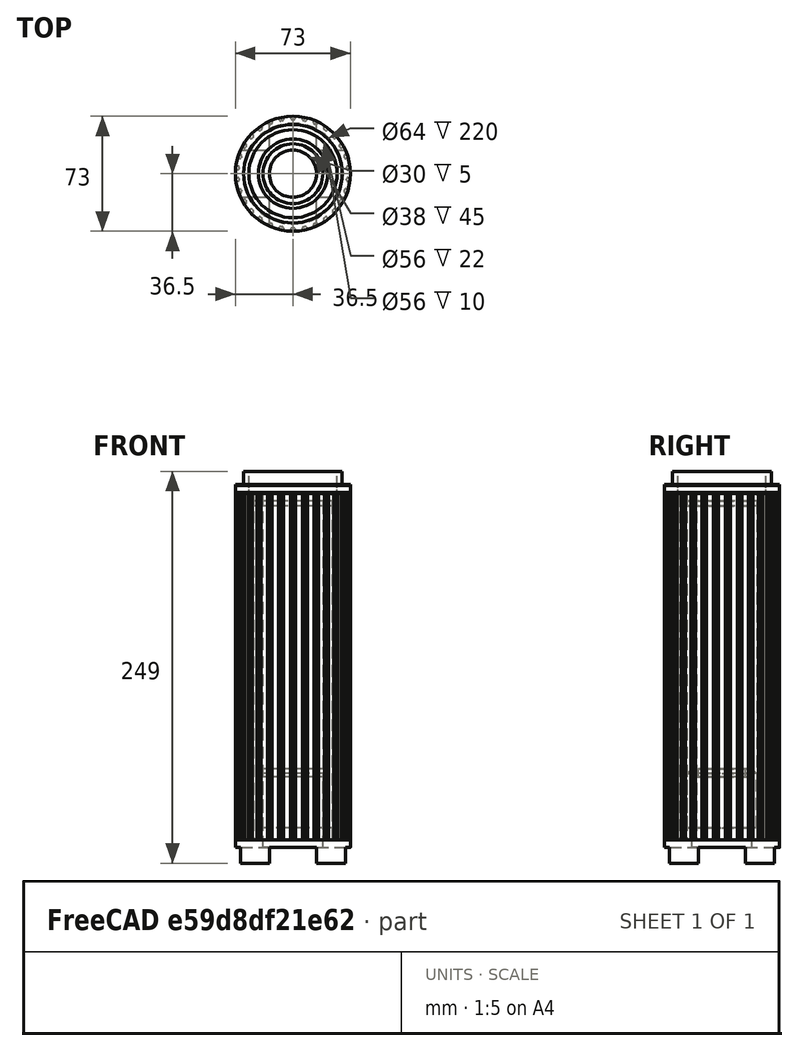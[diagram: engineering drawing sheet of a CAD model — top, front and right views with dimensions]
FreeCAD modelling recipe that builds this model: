
FCSTD DOCUMENT  (FreeCAD 0.15R4671 (Git))
Label: pica-small-v4
License: All rights reserved
LicenseURL: http://en.wikipedia.org/wiki/All_rights_reserved
objects: Part::Cylinder×14, Drawing::FeatureView×10, Part::Cut×7, Part::MultiFuse×6, Drawing::FeatureViewPart×6, Part::Box×2, Part::Part2DObjectPython×1, PartDesign::Pad×1, Drawing::FeaturePage×1, Part::Chamfer×1
note: 33 computed .brp shape members not serialized (recipe doc carries the construction recipe); baked Part::Feature solids carry a one-line shape summary decoded from their .brp

FEATURE [Part::Part2DObjectPython] InvoluteGear  # Draft 2D object (typed FeaturePython)
  ExternalGear = true
  HighPrecision = true
  Modules = 2.5
  NumberOfTeeth = 30
  PressureAngle = 20
FEATURE [PartDesign::Pad] Pad
  Length = 220
  Length2 = 100
  Sketch = -> InvoluteGear
  Type = 0
FEATURE [Part::Cylinder] Cylinder
  Angle = 360
  Height = 240
  Placement = pos=(0,0,-10) rot=(0,0,1;0rad)
  Radius = 32
FEATURE [Part::Cut] Cut  label="Final"
  Base = -> Pad
  Tool = -> Cylinder
FEATURE [Part::Cylinder] Cylinder001
  Angle = 360
  Height = 400
  Radius = 36.5
FEATURE [Part::Cylinder] Cylinder002
  Angle = 360
  Height = 400
  Radius = 100
FEATURE [Part::Cut] Cut001
  Base = -> Cylinder002
  Tool = -> Cylinder001
FEATURE [Part::Cut] Cut002  label="Shade"
  Base = -> Cut
  Placement = pos=(0,0,15) rot=(0,0,1;0rad)
  Tool = -> Cut001
FEATURE [Part::Cylinder] Cylinder003
  Angle = 360
  Height = 15
  Radius = 36.5
FEATURE [Part::Cylinder] Cylinder004
  Angle = 360
  Height = 22.5
  Radius = 31.3
FEATURE [Part::MultiFuse] Fusion  label="Base Fusion"
  Shapes = -> [Cylinder004,Cylinder003]
FEATURE [Drawing::FeatureViewPart] FrontView  label="Shade Side"
  Direction = (0,-1,0)
  HiddenWidth = 0.15
  LineWidth = 0.35
  Rotation = 90
  ShowHiddenLines = true
  ShowSmoothLines = false
  Source = -> Cut002
  Tolerance = 0.05
  ViewResult = <blob: 104580 chars omitted>
  Visible = true
  X = 80
  Y = 270
FEATURE [Drawing::FeatureViewPart] View001  label="Shade Top"
  Direction = (0,0,1)
  HiddenWidth = 0.15
  LineWidth = 0.35
  Rotation = 0
  ShowHiddenLines = false
  ShowSmoothLines = false
  Source = -> Cut002
  Tolerance = 0.05
  ViewResult = <blob: 17331 chars omitted>
  Visible = true
  X = 300
  Y = 80
FEATURE [Drawing::FeatureView] dim006  label="Base Radius"
  Rotation = 0
  ViewResult = <g   >\n <circle cx ="300.000000" cy ="170.000000" r="0.500000" stroke="none" fill="rgb(0,0,0)" /> \n<line x1="255.718312" y1="135.631286" x2="300.000000" y2="170.000000" style="stroke:rgb(0,0,0);stroke-width:0.30" />\n<polygon points="275.273643,150.808927 277.030448,153.438307 278.433561,153.261461 278.256715,151.858348" style="fill:rgb(0,0,0);stroke:rgb(0,0,0);stroke-width:0" />\n<line x1="255.718312" y1="135.631286" x2="231.639949" y2="135.631286" style="stroke:rgb(0,0,0);stroke-width:0.30" />\n<text x="219.448373" y="136.850443" font-family="Arial" font-size="3.6" fill="rgb(0,0,0)" text-anchor="inherit"  >R31.3</text>\n<!--31.3-->\n<!--R%3.3f-->\n</g> 
  Visible = true
  X = 0
  Y = 0
FEATURE [Drawing::FeatureView] centerLines
  Rotation = 0
  ViewResult = <g  transform="scale(1.000000,1.000000)" stroke="rgb(0,0,0)"  stroke-width="0.300000" >\n<path d="M 300.000000,170.000000 L 300.000000,168.000000 M 300.000000,166.000000 L 300.000000,160.000000 M 300.000000,158.000000 L 300.000000,156.000000 "/>\n<path d="M 300.000000,170.000000 L 302.000000,170.000000 M 304.000000,170.000000 L 310.000000,170.000000 M 312.000000,170.000000 L 314.000000,170.000000 "/>\n<path d="M 300.000000,170.000000 L 300.000000,172.000000 M 300.000000,174.000000 L 300.000000,180.000000 M 300.000000,182.000000 L 300.000000,184.000000 "/>\n<path d="M 300.000000,170.000000 L 298.000000,170.000000 M 296.000000,170.000000 L 290.000000,170.000000 M 288.000000,170.000000 L 286.000000,170.000000 "/>\n</g> 
  Visible = true
  X = 0
  Y = 0
FEATURE [Drawing::FeatureView] centerLines001
  Rotation = 0
  ViewResult = <g  transform="scale(1.000000,1.000000)" stroke="rgb(0,0,0)"  stroke-width="0.300000" >\n<path d="M 300.000000,80.000000 L 300.000000,82.000000 M 300.000000,84.000000 L 300.000000,90.000000 M 300.000000,92.000000 L 300.000000,94.000000 "/>\n<path d="M 300.000000,80.000000 L 302.000000,80.000000 M 304.000000,80.000000 L 310.000000,80.000000 M 312.000000,80.000000 L 314.000000,80.000000 "/>\n<path d="M 300.000000,80.000000 L 300.000000,78.000000 M 300.000000,76.000000 L 300.000000,70.000000 M 300.000000,68.000000 L 300.000000,66.000000 "/>\n<path d="M 300.000000,80.000000 L 298.000000,80.000000 M 296.000000,80.000000 L 290.000000,80.000000 M 288.000000,80.000000 L 286.000000,80.000000 "/>\n</g> 
  Visible = true
  X = 0
  Y = 0
FEATURE [Drawing::FeatureView] dim007  label="Shade Radius"
  Rotation = 0
  ViewResult = <g   >\n <circle cx ="300.000000" cy ="80.000000" r="0.500000" stroke="none" fill="rgb(0,0,0)" /> \n<line x1="340.917441" y1="111.884102" x2="300.000000" y2="80.000000" style="stroke:rgb(0,0,0);stroke-width:0.30" />\n<polygon points="325.241495,99.668933 323.489759,97.036174 322.086308,97.210316 322.260451,98.613767" style="fill:rgb(0,0,0);stroke:rgb(0,0,0);stroke-width:0" />\n<line x1="340.917441" y1="111.884102" x2="365.557939" y2="111.884102" style="stroke:rgb(0,0,0);stroke-width:0.30" />\n<text x="369.473360" y="112.835313" font-family="Arial" font-size="3.6" fill="rgb(0,0,0)" text-anchor="inherit"  >R32</text>\n<!--32.0-->\n<!--R%3.3f-->\n</g> 
  Visible = true
  X = 0
  Y = 0
FEATURE [Part::Cylinder] Cylinder005
  Angle = 360
  Height = 90
  Radius = 15
FEATURE [Part::Cylinder] Cylinder006
  Angle = 360
  Height = 55
  Radius = 19
FEATURE [Part::MultiFuse] Fusion002  label="Fixture Mount"
  Shapes = -> [Cylinder005,Cylinder006]
FEATURE [Drawing::FeatureViewPart] View004  label="Base Top"
  Direction = (0,0,1)
  HiddenWidth = 0.15
  LineWidth = 0.35
  Rotation = 0
  ShowHiddenLines = false
  ShowSmoothLines = false
  Tolerance = 0.05
  ViewResult = <g id="Base Top"\n   transform="rotate(0,300,170) translate(300,170) scale(1,1)"\n  >\n<g   stroke="rgb(0, 0, 0)"\n   stroke-width="0.35"\n   stroke-linecap="butt"\n   stroke-linejoin="miter"\n   fill="none"\n   transform="scale(1,-1)"\n  >\n<circle cx ="0" cy ="0" r ="23.3" /><circle cx ="0" cy ="0" r ="15" /><circle cx ="0" cy ="0" r ="31.3" /><circle cx ="0" cy ="0" r ="36.5" /></g>\n</g>
  Visible = true
  X = 300
  Y = 170
FEATURE [Drawing::FeatureViewPart] View005  label="Base Side"
  Direction = (0,-1,0)
  HiddenWidth = 0.15
  LineWidth = 0.35
  Rotation = 90
  ShowHiddenLines = false
  ShowSmoothLines = false
  Tolerance = 0.05
  ViewResult = <blob: 2600 chars omitted>
  Visible = true
  X = 80
  Y = 270
FEATURE [Drawing::FeatureViewPart] View  label="Base Side001"
  Direction = (0,-1,0)
  HiddenWidth = 0.15
  LineWidth = 0.35
  Rotation = 90
  ShowHiddenLines = false
  ShowSmoothLines = false
  Tolerance = 0.05
  ViewResult = <blob: 2605 chars omitted>
  Visible = true
  X = 180
  Y = 100
FEATURE [Drawing::FeatureViewPart] View006  label="Base Top001"
  Direction = (0,0,-1)
  HiddenWidth = 0.15
  LineWidth = 0.35
  Rotation = 0
  ShowHiddenLines = false
  ShowSmoothLines = false
  Tolerance = 0.05
  ViewResult = <blob: 2659 chars omitted>
  Visible = true
  X = 180
  Y = 170
FEATURE [Drawing::FeatureView] dim010  label="dim001"
  Rotation = 0
  ViewResult = <g   >\n<line x1="158.500000" y1="235.000000" x2="177.679727" y2="235.000000" style="stroke:rgb(0,0,0);stroke-width:0.30" />\n<line x1="158.483300" y1="250.000000" x2="177.679727" y2="250.000000" style="stroke:rgb(0,0,0);stroke-width:0.30" />\n<line x1="176.679727" y1="235.000000" x2="176.679727" y2="250.000000" style="stroke:rgb(0,0,0);stroke-width:0.30" />\n<polygon points="176.679727,235.000000 175.679727,238.000000 176.679727,239.000000 177.679727,238.000000" style="fill:rgb(0,0,0);stroke:rgb(0,0,0);stroke-width:0" /><polygon points="176.679727,250.000000 177.679727,247.000000 176.679727,246.000000 175.679727,247.000000" style="fill:rgb(0,0,0);stroke:rgb(0,0,0);stroke-width:0" />\n<text x="183.587709" y="244.783611" font-family="Arial" font-size="3.6" fill="rgb(0,0,0)" text-anchor="inherit" transform="rotate(-90.000000 183.587709,244.783611)" >15</text>\n</g> 
  Visible = true
  X = 0
  Y = 0
FEATURE [Drawing::FeatureView] dim011  label="dim002"
  Rotation = 0
  ViewResult = <g   >\n<line x1="153.300000" y1="228.000000" x2="177.810311" y2="228.000000" style="stroke:rgb(0,0,0);stroke-width:0.30" />\n<line x1="158.500000" y1="235.000000" x2="177.810311" y2="235.000000" style="stroke:rgb(0,0,0);stroke-width:0.30" />\n<line x1="176.810311" y1="228.000000" x2="176.810311" y2="235.000000" style="stroke:rgb(0,0,0);stroke-width:0.30" />\n<polygon points="176.810311,228.000000 177.810311,225.000000 176.810311,224.000000 175.810311,225.000000" style="fill:rgb(0,0,0);stroke:rgb(0,0,0);stroke-width:0" /><polygon points="176.810311,235.000000 175.810311,238.000000 176.810311,239.000000 177.810311,238.000000" style="fill:rgb(0,0,0);stroke:rgb(0,0,0);stroke-width:0" />\n<text x="183.208911" y="232.569545" font-family="Arial" font-size="3.6" fill="rgb(0,0,0)" text-anchor="inherit" transform="rotate(-90.000000 183.208911,232.569545)" >7</text>\n</g> 
  Visible = true
  X = 0
  Y = 0
FEATURE [Drawing::FeatureView] centerLines004
  Rotation = 0
  ViewResult = <g  transform="scale(1.000000,1.000000)" stroke="rgb(0,0,0)"  stroke-width="0.300000" >\n<path d="M 180.000000,169.999925 L 180.000000,167.999925 M 180.000000,165.999925 L 180.000000,159.999925 M 180.000000,157.999925 L 180.000000,155.999925 "/>\n<path d="M 180.000000,169.999925 L 182.000000,169.999925 M 184.000000,169.999925 L 190.000000,169.999925 M 192.000000,169.999925 L 194.000000,169.999925 "/>\n<path d="M 180.000000,169.999925 L 180.000000,171.999925 M 180.000000,173.999925 L 180.000000,179.999925 M 180.000000,181.999925 L 180.000000,183.999925 M 180.000000,185.999925 L 180.000000,186.160469 "/>\n<path d="M 180.000000,169.999925 L 178.000000,169.999925 M 176.000000,169.999925 L 170.000000,169.999925 M 168.000000,169.999925 L 166.583365,169.999925 "/>\n</g> 
  Visible = true
  X = 0
  Y = 0
FEATURE [Drawing::FeatureView] dim
  Rotation = 0
  ViewResult = <g   >\n<line x1="41.500000" y1="25.000000" x2="33.944194" y2="25.000000" style="stroke:rgb(0,0,0);stroke-width:0.30" />\n<line x1="41.500000" y1="245.000000" x2="33.944194" y2="245.000000" style="stroke:rgb(0,0,0);stroke-width:0.30" />\n<line x1="34.944194" y1="25.000000" x2="34.944194" y2="245.000000" style="stroke:rgb(0,0,0);stroke-width:0.30" />\n<polygon points="34.944194,25.000000 33.944194,28.000000 34.944194,29.000000 35.944194,28.000000" style="fill:rgb(0,0,0);stroke:rgb(0,0,0);stroke-width:0" /><polygon points="34.944194,245.000000 35.944194,242.000000 34.944194,241.000000 33.944194,242.000000" style="fill:rgb(0,0,0);stroke:rgb(0,0,0);stroke-width:0" />\n<text x="31.608126" y="136.256650" font-family="Arial" font-size="3.6" fill="rgb(0,0,0)" text-anchor="inherit" transform="rotate(-90.000000 31.608126,136.256650)" >220</text>\n</g> 
  Visible = true
  X = 0
  Y = 0
FEATURE [Drawing::FeatureView] dim012
  Rotation = 0
  ViewResult = <g   >\n<line x1="118.122400" y1="245.000000" x2="126.861722" y2="245.000000" style="stroke:rgb(0,0,0);stroke-width:0.30" />\n<line x1="115.275400" y1="270.000000" x2="126.861722" y2="270.000000" style="stroke:rgb(0,0,0);stroke-width:0.30" />\n<line x1="125.861722" y1="245.000000" x2="125.861722" y2="270.000000" style="stroke:rgb(0,0,0);stroke-width:0.30" />\n<polygon points="125.861722,245.000000 124.861722,248.000000 125.861722,249.000000 126.861722,248.000000" style="fill:rgb(0,0,0);stroke:rgb(0,0,0);stroke-width:0" /><polygon points="125.861722,270.000000 126.861722,267.000000 125.861722,266.000000 124.861722,267.000000" style="fill:rgb(0,0,0);stroke:rgb(0,0,0);stroke-width:0" />\n<text x="132.056471" y="260.197520" font-family="Arial" font-size="3.6" fill="rgb(0,0,0)" text-anchor="inherit" transform="rotate(-90.000000 132.056471,260.197520)" >25</text>\n</g> 
  Visible = true
  X = 0
  Y = 0
FEATURE [Drawing::FeatureView] dim013
  Rotation = 0
  ViewResult = <g   >\n<line x1="143.500000" y1="73.000000" x2="143.500000" y2="45.465562" style="stroke:rgb(0,0,0);stroke-width:0.30" />\n<line x1="216.500000" y1="73.000000" x2="216.500000" y2="45.465562" style="stroke:rgb(0,0,0);stroke-width:0.30" />\n<line x1="143.500000" y1="46.465562" x2="216.500000" y2="46.465562" style="stroke:rgb(0,0,0);stroke-width:0.30" />\n<polygon points="143.500000,46.465562 146.500000,47.465562 147.500000,46.465562 146.500000,45.465562" style="fill:rgb(0,0,0);stroke:rgb(0,0,0);stroke-width:0" /><polygon points="216.500000,46.465562 213.500000,45.465562 212.500000,46.465562 213.500000,47.465562" style="fill:rgb(0,0,0);stroke:rgb(0,0,0);stroke-width:0" />\n<text x="177.413963" y="43.541156" font-family="Arial" font-size="3.6" fill="rgb(0,0,0)" text-anchor="inherit" transform="rotate(0.000000 177.413963,43.541156)" >73</text>\n</g> 
  Visible = true
  X = 0
  Y = 0
FEATURE [Drawing::FeaturePage] AutoDrawing  label="Initial Sketch"
  EditableTexts = FLOYD DIEBEL | 8/22/2015 | 1:1 | 1 | 1 | PICA (SMALL V2) | LAMP WITH SHADE
  Group = -> [FrontView,View001,dim006,centerLines,centerLines001,dim007,View004,View005,dim010,dim011,View,View006,centerLines004,dim,dim012,dim013]
  Template = C:/Program Files/FreeCAD 0.15/data/Mod/Drawing/Templates/A3_Landscape.svg
FEATURE [Part::Cylinder] Cylinder007
  Angle = 360
  Height = 60
  Radius = 22
FEATURE [Part::MultiFuse] Fusion003
  Shapes = -> [Fusion,Cylinder007]
FEATURE [Part::Cut] Cut005  label="Raw"
  Base = -> Fusion003
  Tool = -> Fusion002
FEATURE [Part::Box] Box002  label="Cube002"
  Height = 10
  Length = 100
  Placement = pos=(-50,-15,0) rot=(0,0,1;0rad)
  Width = 30
FEATURE [Part::Box] Box003  label="Cube003"
  Height = 10
  Length = 100
  Placement = pos=(15,-50,0) rot=(0,0,1;1.5708rad)
  Width = 30
FEATURE [Part::MultiFuse] Fusion004  label="Feet Cutout Fusion001"
  Shapes = -> [Box003,Box002]
FEATURE [Part::Cut] Cut006  label="Pre-chamfer"
  Base = -> Cut005
  Tool = -> Fusion004
FEATURE [Part::Chamfer] Chamfer  label="Base"
  Base = -> Cut006
  Edges = 1 edges r=3: [Edge1]
FEATURE [Part::Cylinder] Cylinder008
  Angle = 360
  Height = 5
  Placement = pos=(0,0,8.5) rot=(0,0,1;0rad)
  Radius = 36.5
FEATURE [Part::Cylinder] Cylinder009
  Angle = 360
  Height = 22
  Radius = 31.3
FEATURE [Part::MultiFuse] Fusion005  label="No Cutout"
  Shapes = -> [Cylinder009,Cylinder008]
FEATURE [Part::Cylinder] Cylinder010
  Angle = 360
  Height = 55
  Placement = pos=(0,0,-10) rot=(0,0,1;0rad)
  Radius = 28
FEATURE [Part::Cut] Cut007  label="Joint"
  Base = -> Fusion005
  Placement = pos=(0,0,227) rot=(0,0,1;0rad)
  Tool = -> Cylinder010
FEATURE [Part::Cylinder] Cylinder011
  Angle = 360
  Height = 5
  Placement = pos=(0,0,5) rot=(0,0,1;0rad)
  Radius = 36.5
FEATURE [Part::Cylinder] Cylinder012
  Angle = 360
  Height = 10
  Radius = 31.3
FEATURE [Part::MultiFuse] Fusion006  label="No Cutout001"
  Shapes = -> [Cylinder012,Cylinder011]
FEATURE [Part::Cylinder] Cylinder013
  Angle = 360
  Height = 55
  Placement = pos=(0,0,-10) rot=(0,0,1;0rad)
  Radius = 28
FEATURE [Part::Cut] Cut008  label="Cap"
  Base = -> Fusion006
  Placement = pos=(0,0,230) rot=(0,0,1;0rad)
  Tool = -> Cylinder013
